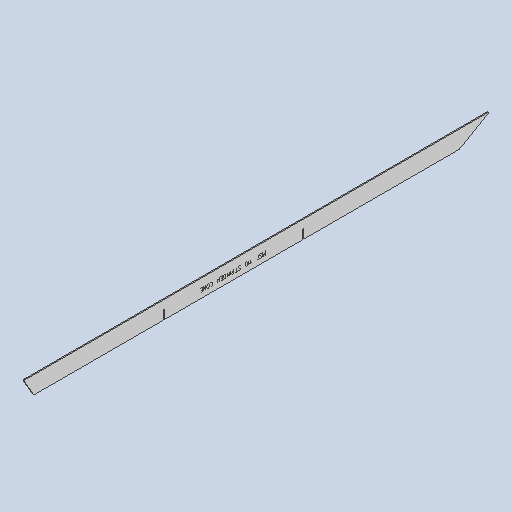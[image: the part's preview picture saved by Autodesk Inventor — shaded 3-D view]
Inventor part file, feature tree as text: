
AUTODESK INVENTOR PART (.ipt)
format: ipt  version: 2025 (Build 290162010, 162A)  size: 231,936 bytes
history: native  units: mm
features: other x5, sketch x3, sheet_metal_op x1, chamfer x1, extrude x1
ambient origin geometry x8: Origin, YZ Plane, XZ Plane, XY Plane, X Axis, Y Axis, Z Axis, Center Point
bodies: Body1 (feature_tree)
feature tree (11):
  sheet_metal_op  "Face1"
  other  "Corner Chamfer1"
  chamfer  "Corner Round1"
  extrude  "Extrusion1"  Depth=1330.0mm
  other  "Mark1"
  other  "A-Side Definition"
  sketch  "Sketch2"  dims[d3=380.0mm d6=380.0mm d7=380.0mm d28=1330.0mm]
  other  "Plate2"
  sketch  "Sketch3"  dims[d29=50.0mm]
  sketch  "Sketch4"  dims[d30=3.0mm d31=6.335545mm d32=10.47518mm d33=3.0mm d34=6.0mm d35=45.0deg d36=10.47518mm d37=6.0mm d38=219.04mm d39=26.0mm d40=3.0mm d41=399.0mm d42=798.0mm d43=3.0mm d44=26.0mm d45=0.0mm d46=0.0mm]
  other  "Definition1"
